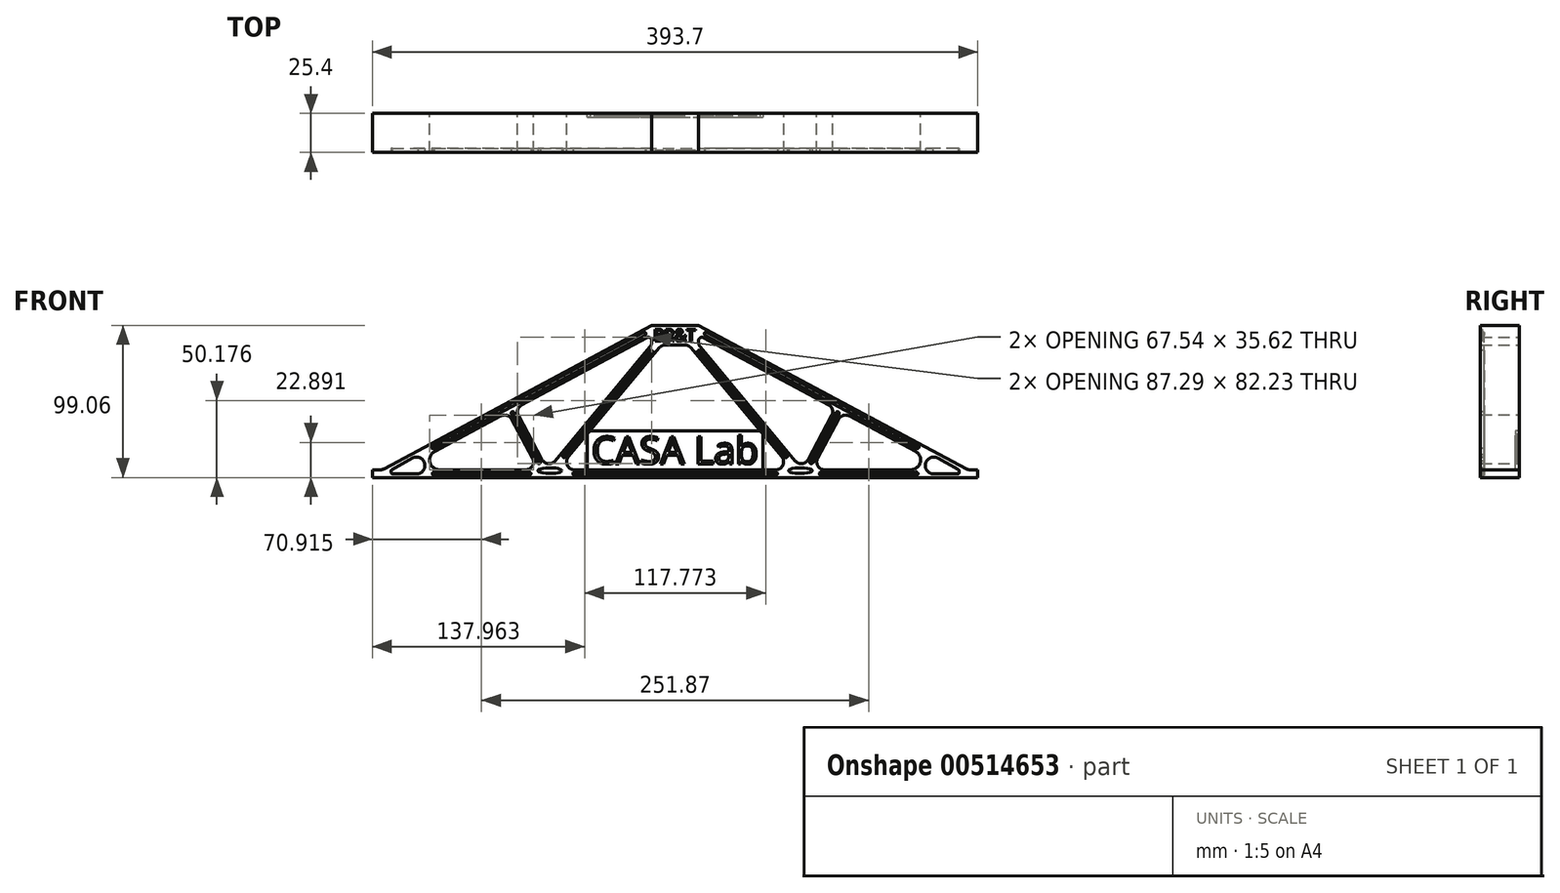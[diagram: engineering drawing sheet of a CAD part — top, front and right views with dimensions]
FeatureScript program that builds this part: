
annotation { "Feature Type Name" : "Feature", "Feature Type Description" : "" }
export const myFeature = defineFeature(function(context is Context, id is Id, definition is map)
    precondition{}
    {
        {
            var Q0;
            Q0=qCreatedBy(makeId("Front.planeOp"),FACE);
            var sketch = newSketch(context, id + "F0", { "sketchPlane" : qUnion([Q0])});
            skLineSegment(sketch, "E0", {"start": v(-15.24, 99.06) * mm, "end": v(0, 99.06) * mm});
            skLineSegment(sketch, "E1.top", {"start": v(-6.25, 86.36) * mm, "end": v(0, 86.36) * mm});
            skLineSegment(sketch, "E1.left", {"start": v(-15.24, 89.18) * mm, "end": v(-15.24, 88.2) * mm});
            skLineSegment(sketch, "E1.right", {"start": v(0, 99.06) * mm, "end": v(0, 86.36) * mm});
            skLineSegment(sketch, "E2.bottom", {"start": v(0, 0) * mm, "end": v(-196.85, 0) * mm});
            skLineSegment(sketch, "E2.top", {"start": v(-97.24, 5.08) * mm, "end": v(-153.38, 5.08) * mm});
            skLineSegment(sketch, "E2.left", {"start": v(0, 0) * mm, "end": v(0, 5.08) * mm});
            skLineSegment(sketch, "E2.right", {"start": v(-196.85, 0) * mm, "end": v(-196.85, 5.08) * mm});
            skLineSegment(sketch, "E3", {"start": v(-15.24, 99.06) * mm, "end": v(-189.38, 5.68) * mm});
            skLineSegment(sketch, "E4", {"start": v(-99.88, 47.32) * mm, "end": v(-18.35, 91.04) * mm});
            skLineSegment(sketch, "E5", {"start": v(-10.15, 84.53) * mm, "end": v(-69.43, 13.41) * mm});
            skLineSegment(sketch, "E6", {"start": v(-76.38, 5.08) * mm, "end": v(-82.99, 5.08) * mm});
            skLineSegment(sketch, "E7", {"start": v(-78.17, 10.86) * mm, "end": v(-16.42, 84.95) * mm});
            skLineSegment(sketch, "E8", {"start": v(-86.55, 11.72) * mm, "end": v(-101.95, 40.45) * mm});
            skLineSegment(sketch, "E9", {"start": v(-106.43, 38.05) * mm, "end": v(-92.77, 12.56) * mm});
            skLineSegment(sketch, "E10", {"start": v(-88.75, 5.08) * mm, "end": v(-82.99, 5.08) * mm});
            skArc(sketch, "E11.filletArc", {"start": v(-156.38, 17.03) * mm, "mid": v(-159.54, 9.88) * mm, "end": v(-153.38, 5.08) * mm});
            skLineSegment(sketch, "E12", {"start": v(-196.85, 5.08) * mm, "end": v(-191.78, 5.08) * mm});
            skPoint(sketch, "E13.newPointA", {"position": v(-15.24, 92.71) * mm});
            skPoint(sketch, "E13.newPointB", {"position": v(-15.24, 99.06) * mm});
            skArc(sketch, "E13.filletArc", {"start": v(-15.24, 89.18) * mm, "mid": v(-16.27, 91) * mm, "end": v(-18.35, 91.04) * mm});
            skPoint(sketch, "E14.visualSharp", {"position": v(-82.99, 5.08) * mm});
            skArc(sketch, "E14.filletArc", {"start": v(-86.55, 11.72) * mm, "mid": v(-82.58, 9.06) * mm, "end": v(-78.17, 10.86) * mm});
            skArc(sketch, "E15.filletArc", {"start": v(-99.88, 47.32) * mm, "mid": v(-102.34, 44.32) * mm, "end": v(-101.95, 40.45) * mm});
            skLineSegment(sketch, "E16", {"start": v(-113.3, 40.12) * mm, "end": v(-156.38, 17.03) * mm});
            skPoint(sketch, "E17.visualSharp", {"position": v(-108.83, 42.52) * mm});
            skArc(sketch, "E17.filletArc", {"start": v(-106.43, 38.05) * mm, "mid": v(-109.44, 40.5) * mm, "end": v(-113.3, 40.12) * mm});
            skPoint(sketch, "E18.newPointA", {"position": v(-88.75, 5.08) * mm});
            skArc(sketch, "E18.filletArc", {"start": v(-97.24, 5.08) * mm, "mid": v(-92.88, 7.55) * mm, "end": v(-92.77, 12.56) * mm});
            skLineSegment(sketch, "E19", {"start": v(-65.53, 5.08) * mm, "end": v(0, 5.08) * mm});
            skPoint(sketch, "E20.visualSharp", {"position": v(-76.38, 5.08) * mm});
            skArc(sketch, "E20.filletArc", {"start": v(-69.43, 13.41) * mm, "mid": v(-70.13, 8) * mm, "end": v(-65.53, 5.08) * mm});
            skArc(sketch, "E21.filletArc", {"start": v(-6.25, 86.36) * mm, "mid": v(-8.4, 85.88) * mm, "end": v(-10.15, 84.53) * mm});
            skLineSegment(sketch, "E22.MirrorCS", {"start": v(15.24, 89.18) * mm, "end": v(15.24, 88.2) * mm});
            skArc(sketch, "E23.MirrorCS", {"start": v(15.24, 89.18) * mm, "mid": v(16.27, 91) * mm, "end": v(18.35, 91.04) * mm});
            skArc(sketch, "E24.MirrorCS", {"start": v(86.55, 11.72) * mm, "mid": v(82.58, 9.06) * mm, "end": v(78.17, 10.86) * mm});
            skLineSegment(sketch, "E25.MirrorCS", {"start": v(196.85, 5.08) * mm, "end": v(191.78, 5.08) * mm});
            skLineSegment(sketch, "E26.MirrorCS", {"start": v(76.38, 5.08) * mm, "end": v(82.99, 5.08) * mm});
            skArc(sketch, "E27.MirrorCS", {"start": v(6.25, 86.36) * mm, "mid": v(8.4, 85.88) * mm, "end": v(10.15, 84.53) * mm});
            skLineSegment(sketch, "E28.MirrorCS", {"start": v(196.85, 0) * mm, "end": v(196.85, 5.08) * mm});
            skArc(sketch, "E29.MirrorCS", {"start": v(106.43, 38.05) * mm, "mid": v(109.44, 40.5) * mm, "end": v(113.3, 40.12) * mm});
            skLineSegment(sketch, "E30.MirrorCS", {"start": v(6.25, 86.36) * mm, "end": v(0, 86.36) * mm});
            skLineSegment(sketch, "E31.MirrorCS", {"start": v(88.75, 5.08) * mm, "end": v(82.99, 5.08) * mm});
            skArc(sketch, "E32.MirrorCS", {"start": v(97.24, 5.08) * mm, "mid": v(92.88, 7.55) * mm, "end": v(92.77, 12.56) * mm});
            skArc(sketch, "E33.MirrorCS", {"start": v(99.88, 47.32) * mm, "mid": v(102.34, 44.32) * mm, "end": v(101.95, 40.45) * mm});
            skArc(sketch, "E34.MirrorCS", {"start": v(69.43, 13.41) * mm, "mid": v(70.13, 8) * mm, "end": v(65.53, 5.08) * mm});
            skLineSegment(sketch, "E35.MirrorCS", {"start": v(15.24, 99.06) * mm, "end": v(0, 99.06) * mm});
            skPoint(sketch, "E36.MirrorP", {"position": v(15.24, 92.71) * mm});
            skLineSegment(sketch, "E37.MirrorCS", {"start": v(97.24, 5.08) * mm, "end": v(153.38, 5.08) * mm});
            skPoint(sketch, "E38.MirrorP", {"position": v(76.38, 5.08) * mm});
            skLineSegment(sketch, "E39.MirrorCS", {"start": v(0, 0) * mm, "end": v(196.85, 0) * mm});
            skLineSegment(sketch, "E40.MirrorCS", {"start": v(65.53, 5.08) * mm, "end": v(0, 5.08) * mm});
            skLineSegment(sketch, "E41.MirrorCS", {"start": v(113.3, 40.12) * mm, "end": v(156.38, 17.03) * mm});
            skLineSegment(sketch, "E42.MirrorCS", {"start": v(99.88, 47.32) * mm, "end": v(18.35, 91.04) * mm});
            skLineSegment(sketch, "E43.MirrorCS", {"start": v(10.15, 84.53) * mm, "end": v(69.43, 13.41) * mm});
            skLineSegment(sketch, "E44.MirrorCS", {"start": v(15.24, 99.06) * mm, "end": v(189.38, 5.68) * mm});
            skPoint(sketch, "E45.MirrorP", {"position": v(108.83, 42.52) * mm});
            skLineSegment(sketch, "E46.MirrorCS", {"start": v(106.43, 38.05) * mm, "end": v(92.77, 12.56) * mm});
            skLineSegment(sketch, "E47.MirrorCS", {"start": v(86.55, 11.72) * mm, "end": v(101.95, 40.45) * mm});
            skPoint(sketch, "E48.MirrorP", {"position": v(88.75, 5.08) * mm});
            skArc(sketch, "E49.MirrorCS", {"start": v(156.38, 17.03) * mm, "mid": v(159.54, 9.88) * mm, "end": v(153.38, 5.08) * mm});
            skPoint(sketch, "E50.MirrorP", {"position": v(82.99, 5.08) * mm});
            skPoint(sketch, "E51.MirrorP", {"position": v(15.24, 99.06) * mm});
            skLineSegment(sketch, "E52.MirrorCS", {"start": v(78.17, 10.86) * mm, "end": v(16.42, 84.95) * mm});
            skPoint(sketch, "E53.visualSharp", {"position": v(-15.24, 86.36) * mm});
            skArc(sketch, "E53.filletArc", {"start": v(-16.42, 84.95) * mm, "mid": v(-15.54, 86.47) * mm, "end": v(-15.24, 88.2) * mm});
            skPoint(sketch, "E54.visualSharp", {"position": v(15.24, 86.36) * mm});
            skArc(sketch, "E54.filletArc", {"start": v(15.24, 88.2) * mm, "mid": v(15.54, 86.47) * mm, "end": v(16.42, 84.95) * mm});
            skPoint(sketch, "E55.visualSharp", {"position": v(-190.5, 5.08) * mm});
            skArc(sketch, "E55.filletArc", {"start": v(-191.78, 5.08) * mm, "mid": v(-190.54, 5.23) * mm, "end": v(-189.38, 5.68) * mm});
            skPoint(sketch, "E56.visualSharp", {"position": v(190.5, 5.08) * mm});
            skArc(sketch, "E56.filletArc", {"start": v(189.38, 5.68) * mm, "mid": v(190.54, 5.23) * mm, "end": v(191.78, 5.08) * mm});
            skSolve(sketch);
        }
        {
            var Q0;
            Q0=makeQuery(id+"F0.imprint","IMPRINT",FACE,{"disambiguationData":[TD([[makeQuery(id+"F0.imprint","IMPRINT",EDGE,{"derivedFrom":sQuery(id+"F0.wireOp",EDGE,"E0")}),-1.0]])]});
            var Q1;
            Q1=makeQuery(id+"F0.imprint","IMPRINT",FACE,{"disambiguationData":[TD([[makeQuery(id+"F0.imprint","IMPRINT",EDGE,{"derivedFrom":sQuery(id+"F0.wireOp",EDGE,"E22.MirrorCS")}),-1.0]])]});
            extrude(context, id + "F1", {"entities" : qUnion([Q0, Q1]), "depth" : 25.4 * mm, "offsetDistance" : 25.4 * mm});
        }
        {
            var Q0;
            Q0=makeQuery(id+"F1.opExtrude","CAP_FACE",FACE,{"disambiguationData":[OSD([sQuery(id+"F0.wireOp",EDGE,"E0"),sQuery(id+"F0.wireOp",EDGE,"E1.top"),sQuery(id+"F0.wireOp",EDGE,"E1.left"),sQuery(id+"F0.wireOp",EDGE,"E2.bottom"),sQuery(id+"F0.wireOp",EDGE,"E2.top"),sQuery(id+"F0.wireOp",EDGE,"E2.right"),sQuery(id+"F0.wireOp",EDGE,"E3"),sQuery(id+"F0.wireOp",EDGE,"E4"),sQuery(id+"F0.wireOp",EDGE,"E5"),sQuery(id+"F0.wireOp",EDGE,"E7"),sQuery(id+"F0.wireOp",EDGE,"E8"),sQuery(id+"F0.wireOp",EDGE,"E9"),sQuery(id+"F0.wireOp",EDGE,"E11.filletArc"),sQuery(id+"F0.wireOp",EDGE,"E12"),sQuery(id+"F0.wireOp",EDGE,"E13.filletArc"),sQuery(id+"F0.wireOp",EDGE,"E14.filletArc"),sQuery(id+"F0.wireOp",EDGE,"E15.filletArc"),sQuery(id+"F0.wireOp",EDGE,"E16"),sQuery(id+"F0.wireOp",EDGE,"E17.filletArc"),sQuery(id+"F0.wireOp",EDGE,"E18.filletArc"),sQuery(id+"F0.wireOp",EDGE,"E19"),sQuery(id+"F0.wireOp",EDGE,"E20.filletArc"),sQuery(id+"F0.wireOp",EDGE,"E21.filletArc"),sQuery(id+"F0.wireOp",EDGE,"E22.MirrorCS"),sQuery(id+"F0.wireOp",EDGE,"E23.MirrorCS"),sQuery(id+"F0.wireOp",EDGE,"E24.MirrorCS"),sQuery(id+"F0.wireOp",EDGE,"E25.MirrorCS"),sQuery(id+"F0.wireOp",EDGE,"E27.MirrorCS"),sQuery(id+"F0.wireOp",EDGE,"E28.MirrorCS"),sQuery(id+"F0.wireOp",EDGE,"E29.MirrorCS"),sQuery(id+"F0.wireOp",EDGE,"E30.MirrorCS"),sQuery(id+"F0.wireOp",EDGE,"E32.MirrorCS"),sQuery(id+"F0.wireOp",EDGE,"E33.MirrorCS"),sQuery(id+"F0.wireOp",EDGE,"E34.MirrorCS"),sQuery(id+"F0.wireOp",EDGE,"E37.MirrorCS"),sQuery(id+"F0.wireOp",EDGE,"E39.MirrorCS"),sQuery(id+"F0.wireOp",EDGE,"E40.MirrorCS"),sQuery(id+"F0.wireOp",EDGE,"E41.MirrorCS"),sQuery(id+"F0.wireOp",EDGE,"E42.MirrorCS"),sQuery(id+"F0.wireOp",EDGE,"E43.MirrorCS"),sQuery(id+"F0.wireOp",EDGE,"E44.MirrorCS"),sQuery(id+"F0.wireOp",EDGE,"E46.MirrorCS"),sQuery(id+"F0.wireOp",EDGE,"E47.MirrorCS"),sQuery(id+"F0.wireOp",EDGE,"E35.MirrorCS"),sQuery(id+"F0.wireOp",EDGE,"E49.MirrorCS"),sQuery(id+"F0.wireOp",EDGE,"E52.MirrorCS")])],"isStart":false});
            var sketch = newSketch(context, id + "F2", { "sketchPlane" : qUnion([Q0])});
            skText(sketch, "E57", { "text": "BR&T", "fontName": "OpenSans-Regular.ttf"});
            const initialGuessF2  = {"E57": [-0.01397, 0.0888, 1, 0, 0.00772]};
            skSetInitialGuess(sketch, initialGuessF2);
            skSolve(sketch);
        }
        {
            var Q0;
            Q0 = qSketchRegion(id + "F2", true);
            extrude(context, id + "F3", {"entities" : qUnion([Q0]), "operationType" : NewBodyOperationType.REMOVE, "oppositeDirection" : true, "depth" : 1.27 * mm, "offsetDistance" : 25.4 * mm});
        }
        {
            var Q0;
            Q0=qCreatedBy(makeId("Front.planeOp"),FACE);
            var sketch = newSketch(context, id + "F4", { "sketchPlane" : qUnion([Q0])});
            skLineSegment(sketch, "E58.bottom", {"start": v(-57.15, 5.08) * mm, "end": v(0, 5.08) * mm});
            skLineSegment(sketch, "E58.top", {"start": v(-57.15, 30.48) * mm, "end": v(0, 30.48) * mm});
            skLineSegment(sketch, "E58.left", {"start": v(-57.15, 5.08) * mm, "end": v(-57.15, 30.48) * mm});
            skLineSegment(sketch, "E58.right", {"start": v(0, 5.08) * mm, "end": v(0, 30.48) * mm});
            skLineSegment(sketch, "E59.MirrorCS", {"start": v(57.15, 5.08) * mm, "end": v(57.15, 30.48) * mm});
            skLineSegment(sketch, "E60.MirrorCS", {"start": v(57.15, 30.48) * mm, "end": v(0, 30.48) * mm});
            skLineSegment(sketch, "E61.MirrorCS", {"start": v(57.15, 5.08) * mm, "end": v(0, 5.08) * mm});
            skSolve(sketch);
        }
        {
            var Q0;
            Q0 = qSketchRegion(id + "F4", true);
            extrude(context, id + "F5", {"entities" : qUnion([Q0]), "operationType" : NewBodyOperationType.ADD, "depth" : 2.54 * mm, "offsetDistance" : 25.4 * mm});
        }
        {
            var Q0;
            Q0=makeQuery(id+"F5.opExtrude","CAP_FACE",FACE,{"disambiguationData":[OSD([sQuery(id+"F4.wireOp",EDGE,"E58.bottom"),sQuery(id+"F4.wireOp",EDGE,"E58.top"),sQuery(id+"F4.wireOp",EDGE,"E58.left"),sQuery(id+"F4.wireOp",EDGE,"E59.MirrorCS"),sQuery(id+"F4.wireOp",EDGE,"E60.MirrorCS"),sQuery(id+"F4.wireOp",EDGE,"E61.MirrorCS")])],"isStart":false});
            var sketch = newSketch(context, id + "F6", { "sketchPlane" : qUnion([Q0])});
            skText(sketch, "E62", { "text": "CASA Lab", "fontName": "OpenSans-Regular.ttf"});
            const initialGuessF6  = {"E62": [-0.05436, 0.0089, 1, 0, 0.01778]};
            skSetInitialGuess(sketch, initialGuessF6);
            skSolve(sketch);
        }
        {
            var Q0;
            Q0 = qSketchRegion(id + "F6", true);
            extrude(context, id + "F7", {"entities" : qUnion([Q0]), "operationType" : NewBodyOperationType.REMOVE, "oppositeDirection" : true, "depth" : 1.27 * mm, "offsetDistance" : 25.4 * mm});
        }
        {
            var Q0;
            {var subQ0=sQuery(id+"F0.wireOp",EDGE,"E32.MirrorCS");var subQ1=sQuery(id+"F0.wireOp",EDGE,"E20.filletArc");var subQ2=sQuery(id+"F0.wireOp",EDGE,"E29.MirrorCS");var subQ3=sQuery(id+"F0.wireOp",EDGE,"E40.MirrorCS");var subQ4=sQuery(id+"F0.wireOp",EDGE,"E19");var subQ5=sQuery(id+"F0.wireOp",EDGE,"E28.MirrorCS");var subQ6=sQuery(id+"F0.wireOp",EDGE,"E18.filletArc");var subQ7=sQuery(id+"F0.wireOp",EDGE,"E17.filletArc");var subQ8=sQuery(id+"F0.wireOp",EDGE,"E16");var subQ9=sQuery(id+"F0.wireOp",EDGE,"E24.MirrorCS");var subQ10=sQuery(id+"F0.wireOp",EDGE,"E15.filletArc");var subQ11=sQuery(id+"F0.wireOp",EDGE,"E14.filletArc");var subQ12=sQuery(id+"F0.wireOp",EDGE,"E13.filletArc");var subQ13=sQuery(id+"F0.wireOp",EDGE,"E12");var subQ14=sQuery(id+"F0.wireOp",EDGE,"E11.filletArc");var subQ15=sQuery(id+"F0.wireOp",EDGE,"E9");var subQ16=sQuery(id+"F0.wireOp",EDGE,"E8");var subQ17=sQuery(id+"F0.wireOp",EDGE,"E39.MirrorCS");var subQ18=sQuery(id+"F0.wireOp",EDGE,"E2.bottom");var subQ19=sQuery(id+"F0.wireOp",EDGE,"E1.left");var subQ20=sQuery(id+"F0.wireOp",EDGE,"E30.MirrorCS");var subQ21=sQuery(id+"F0.wireOp",EDGE,"E1.top");var subQ22=sQuery(id+"F0.wireOp",EDGE,"E35.MirrorCS");var subQ23=sQuery(id+"F0.wireOp",EDGE,"E0");var subQ24=sQuery(id+"F0.wireOp",EDGE,"E2.top");var subQ25=sQuery(id+"F0.wireOp",EDGE,"E2.right");var subQ26=sQuery(id+"F0.wireOp",EDGE,"E3");var subQ27=sQuery(id+"F0.wireOp",EDGE,"E4");var subQ28=sQuery(id+"F0.wireOp",EDGE,"E5");var subQ29=sQuery(id+"F0.wireOp",EDGE,"E7");var subQ30=sQuery(id+"F0.wireOp",EDGE,"E33.MirrorCS");var subQ31=sQuery(id+"F0.wireOp",EDGE,"E21.filletArc");var subQ32=sQuery(id+"F0.wireOp",EDGE,"E34.MirrorCS");var subQ33=sQuery(id+"F0.wireOp",EDGE,"E22.MirrorCS");var subQ34=sQuery(id+"F0.wireOp",EDGE,"E37.MirrorCS");var subQ35=sQuery(id+"F0.wireOp",EDGE,"E23.MirrorCS");var subQ36=sQuery(id+"F0.wireOp",EDGE,"E41.MirrorCS");var subQ37=sQuery(id+"F0.wireOp",EDGE,"E42.MirrorCS");var subQ38=sQuery(id+"F0.wireOp",EDGE,"E25.MirrorCS");var subQ39=sQuery(id+"F0.wireOp",EDGE,"E43.MirrorCS");var subQ40=sQuery(id+"F0.wireOp",EDGE,"E27.MirrorCS");var subQ41=sQuery(id+"F0.wireOp",EDGE,"E44.MirrorCS");var subQ42=sQuery(id+"F0.wireOp",EDGE,"E46.MirrorCS");var subQ43=sQuery(id+"F0.wireOp",EDGE,"E47.MirrorCS");var subQ44=sQuery(id+"F0.wireOp",EDGE,"E49.MirrorCS");var subQ45=sQuery(id+"F0.wireOp",EDGE,"E52.MirrorCS");var subQ46=sQuery(id+"F0.wireOp",EDGE,"E53.filletArc");var subQ47=sQuery(id+"F0.wireOp",EDGE,"E54.filletArc");var subQ48=sQuery(id+"F0.wireOp",EDGE,"E55.filletArc");var subQ49=sQuery(id+"F0.wireOp",EDGE,"E56.filletArc");Q0=makeQuery(id+"F3.boolean.opBoolean","SPLIT",FACE,{"disambiguationData":[TD([makeQuery(id+"F1.opExtrude","SWEPT_FACE",FACE,{"disambiguationData":[OSD([subQ19])]})])],"derivedFrom":makeQuery(id+"F1.opExtrude","CAP_FACE",FACE,{"disambiguationData":[OSD([subQ23,subQ21,subQ19,subQ18,subQ24,subQ25,subQ26,subQ27,subQ28,subQ29,subQ16,subQ15,subQ14,subQ13,subQ12,subQ11,subQ10,subQ8,subQ7,subQ6,subQ4,subQ1,subQ31,subQ33,subQ35,subQ9,subQ38,subQ40,subQ5,subQ2,subQ20,subQ0,subQ30,subQ32,subQ34,subQ17,subQ3,subQ36,subQ37,subQ39,subQ41,subQ42,subQ43,subQ22,subQ44,subQ45,subQ46,subQ47,subQ48,subQ49])],"isStart":false})});}
            var sketch = newSketch(context, id + "F8", { "sketchPlane" : qUnion([Q0])});
            skEllipse(sketch, "E63", {"center": v(-81.48, 4.48) * mm, "majorRadius": 7.68 * mm, "minorRadius": 1.86 * mm, "majorAxis": v(1, 0)});
            skLineSegment(sketch, "E64", {"start": v(-157.1, 18.96) * mm, "end": v(-19.46, 92.76) * mm});
            skLineSegment(sketch, "E65", {"start": v(-157.1, 18.96) * mm, "end": v(-158.06, 20.75) * mm});
            skLineSegment(sketch, "E66", {"start": v(-158.06, 20.75) * mm, "end": v(-20.56, 94.48) * mm});
            skLineSegment(sketch, "E67", {"start": v(-20.56, 94.48) * mm, "end": v(-19.46, 92.76) * mm});
            skArc(sketch, "E68", {"start": v(-158.06, 20.75) * mm, "mid": v(-158.48, 19.37) * mm, "end": v(-157.1, 18.96) * mm});
            skArc(sketch, "E69", {"start": v(-19.46, 92.76) * mm, "mid": v(-19.21, 94.13) * mm, "end": v(-20.56, 94.48) * mm});
            skLineSegment(sketch, "E70", {"start": v(-104.72, 42.37) * mm, "end": v(-87.68, 10.6) * mm});
            skLineSegment(sketch, "E71", {"start": v(-104.72, 42.37) * mm, "end": v(-106.5, 41.41) * mm});
            skLineSegment(sketch, "E72", {"start": v(-106.5, 41.41) * mm, "end": v(-89.44, 9.58) * mm});
            skLineSegment(sketch, "E73", {"start": v(-89.44, 9.58) * mm, "end": v(-87.68, 10.6) * mm});
            skArc(sketch, "E74", {"start": v(-104.72, 42.37) * mm, "mid": v(-106.1, 42.79) * mm, "end": v(-106.5, 41.41) * mm});
            skArc(sketch, "E75", {"start": v(-89.44, 9.58) * mm, "mid": v(-88.03, 9.18) * mm, "end": v(-87.68, 10.6) * mm});
            skLineSegment(sketch, "E76", {"start": v(-72.98, 14.7) * mm, "end": v(-16.42, 82.57) * mm});
            skLineSegment(sketch, "E77", {"start": v(-16.42, 82.57) * mm, "end": v(-14.86, 81.27) * mm});
            skLineSegment(sketch, "E78", {"start": v(-14.86, 81.27) * mm, "end": v(-71.41, 13.41) * mm});
            skLineSegment(sketch, "E79", {"start": v(-71.41, 13.41) * mm, "end": v(-72.98, 14.7) * mm});
            skArc(sketch, "E80", {"start": v(-14.86, 81.27) * mm, "mid": v(-14.99, 82.7) * mm, "end": v(-16.42, 82.57) * mm});
            skArc(sketch, "E81", {"start": v(-72.98, 14.7) * mm, "mid": v(-72.84, 13.28) * mm, "end": v(-71.41, 13.41) * mm});
            skLineSegment(sketch, "E82", {"start": v(-156.81, 3.56) * mm, "end": v(-94.84, 3.56) * mm});
            skLineSegment(sketch, "E83", {"start": v(-94.84, 3.56) * mm, "end": v(-94.84, 1.52) * mm});
            skLineSegment(sketch, "E84", {"start": v(-94.84, 1.52) * mm, "end": v(-156.94, 1.52) * mm});
            skLineSegment(sketch, "E85", {"start": v(-156.94, 1.52) * mm, "end": v(-156.81, 3.56) * mm});
            skArc(sketch, "E86", {"start": v(-156.81, 3.56) * mm, "mid": v(-157.96, 2.6) * mm, "end": v(-156.94, 1.52) * mm});
            skArc(sketch, "E87", {"start": v(-94.84, 1.52) * mm, "mid": v(-93.83, 2.54) * mm, "end": v(-94.84, 3.56) * mm});
            skLineSegment(sketch, "E88", {"start": v(-183.96, 5.45) * mm, "end": v(-171, 12.66) * mm});
            skLineSegment(sketch, "E89", {"start": v(-184.04, 2.35) * mm, "end": v(-167.52, 2.35) * mm});
            skArc(sketch, "E90", {"start": v(-183.96, 5.45) * mm, "mid": v(-184.89, 3.92) * mm, "end": v(-184.04, 2.35) * mm});
            skArc(sketch, "E91", {"start": v(-167.52, 2.35) * mm, "mid": v(-163.07, 9.6) * mm, "end": v(-171, 12.66) * mm});
            skLineSegment(sketch, "E92", {"start": v(0, 3.56) * mm, "end": v(-65.53, 3.56) * mm});
            skLineSegment(sketch, "E93", {"start": v(-65.53, 3.56) * mm, "end": v(-65.53, 1.52) * mm});
            skLineSegment(sketch, "E94", {"start": v(-65.53, 1.52) * mm, "end": v(0, 1.52) * mm});
            skArc(sketch, "E95", {"start": v(-65.53, 3.56) * mm, "mid": v(-66.54, 2.54) * mm, "end": v(-65.53, 1.52) * mm});
            skArc(sketch, "E96.MirrorCS", {"start": v(72.98, 14.7) * mm, "mid": v(72.84, 13.28) * mm, "end": v(71.41, 13.41) * mm});
            skLineSegment(sketch, "E97.MirrorCS", {"start": v(16.42, 82.57) * mm, "end": v(14.86, 81.27) * mm});
            skArc(sketch, "E98.MirrorCS", {"start": v(14.86, 81.27) * mm, "mid": v(14.99, 82.7) * mm, "end": v(16.42, 82.57) * mm});
            skLineSegment(sketch, "E99.MirrorCS", {"start": v(157.1, 18.96) * mm, "end": v(158.06, 20.75) * mm});
            skLineSegment(sketch, "E100.MirrorCS", {"start": v(71.41, 13.41) * mm, "end": v(72.98, 14.7) * mm});
            skLineSegment(sketch, "E101.MirrorCS", {"start": v(156.94, 1.52) * mm, "end": v(156.81, 3.56) * mm});
            skArc(sketch, "E102.MirrorCS", {"start": v(158.06, 20.75) * mm, "mid": v(158.48, 19.37) * mm, "end": v(157.1, 18.96) * mm});
            skLineSegment(sketch, "E103.MirrorCS", {"start": v(94.84, 3.56) * mm, "end": v(94.84, 1.52) * mm});
            skLineSegment(sketch, "E104.MirrorCS", {"start": v(104.72, 42.37) * mm, "end": v(106.5, 41.41) * mm});
            skArc(sketch, "E105.MirrorCS", {"start": v(94.84, 1.52) * mm, "mid": v(93.83, 2.54) * mm, "end": v(94.84, 3.56) * mm});
            skArc(sketch, "E106.MirrorCS", {"start": v(156.81, 3.56) * mm, "mid": v(157.96, 2.6) * mm, "end": v(156.94, 1.52) * mm});
            skLineSegment(sketch, "E107.MirrorCS", {"start": v(89.44, 9.58) * mm, "end": v(87.68, 10.6) * mm});
            skArc(sketch, "E108.MirrorCS", {"start": v(104.72, 42.37) * mm, "mid": v(106.1, 42.79) * mm, "end": v(106.5, 41.41) * mm});
            skArc(sketch, "E109.MirrorCS", {"start": v(65.53, 3.56) * mm, "mid": v(66.54, 2.54) * mm, "end": v(65.53, 1.52) * mm});
            skLineSegment(sketch, "E110.MirrorCS", {"start": v(20.56, 94.48) * mm, "end": v(19.46, 92.76) * mm});
            skLineSegment(sketch, "E111.MirrorCS", {"start": v(65.53, 3.56) * mm, "end": v(65.53, 1.52) * mm});
            skArc(sketch, "E112.MirrorCS", {"start": v(19.46, 92.76) * mm, "mid": v(19.21, 94.13) * mm, "end": v(20.56, 94.48) * mm});
            skArc(sketch, "E113.MirrorCS", {"start": v(89.44, 9.58) * mm, "mid": v(88.03, 9.18) * mm, "end": v(87.68, 10.6) * mm});
            skArc(sketch, "E114.MirrorCS", {"start": v(183.96, 5.45) * mm, "mid": v(184.89, 3.92) * mm, "end": v(184.04, 2.35) * mm});
            skLineSegment(sketch, "E115.MirrorCS", {"start": v(72.98, 14.7) * mm, "end": v(16.42, 82.57) * mm});
            skLineSegment(sketch, "E116.MirrorCS", {"start": v(14.86, 81.27) * mm, "end": v(71.41, 13.41) * mm});
            skEllipse(sketch, "E117.MirrorC", {"center": v(81.48, 4.48) * mm, "majorRadius": 7.68 * mm, "minorRadius": 1.86 * mm, "majorAxis": v(-1, 0)});
            skLineSegment(sketch, "E118.MirrorCS", {"start": v(157.1, 18.96) * mm, "end": v(19.46, 92.76) * mm});
            skLineSegment(sketch, "E119.MirrorCS", {"start": v(106.5, 41.41) * mm, "end": v(89.44, 9.58) * mm});
            skLineSegment(sketch, "E120.MirrorCS", {"start": v(158.06, 20.75) * mm, "end": v(20.56, 94.48) * mm});
            skLineSegment(sketch, "E121.MirrorCS", {"start": v(183.96, 5.45) * mm, "end": v(171, 12.66) * mm});
            skLineSegment(sketch, "E122.MirrorCS", {"start": v(65.53, 1.52) * mm, "end": v(0, 1.52) * mm});
            skArc(sketch, "E123.MirrorCS", {"start": v(167.52, 2.35) * mm, "mid": v(163.07, 9.6) * mm, "end": v(171, 12.66) * mm});
            skLineSegment(sketch, "E124.MirrorCS", {"start": v(0, 3.56) * mm, "end": v(65.53, 3.56) * mm});
            skLineSegment(sketch, "E125.MirrorCS", {"start": v(104.72, 42.37) * mm, "end": v(87.68, 10.6) * mm});
            skLineSegment(sketch, "E126.MirrorCS", {"start": v(94.84, 1.52) * mm, "end": v(156.94, 1.52) * mm});
            skLineSegment(sketch, "E127.MirrorCS", {"start": v(156.81, 3.56) * mm, "end": v(94.84, 3.56) * mm});
            skLineSegment(sketch, "E128.MirrorCS", {"start": v(184.04, 2.35) * mm, "end": v(167.52, 2.35) * mm});
            skSolve(sketch);
        }
        {
            var Q0;
            Q0 = qSketchRegion(id + "F8", true);
            extrude(context, id + "F9", {"entities" : qUnion([Q0]), "operationType" : NewBodyOperationType.REMOVE, "oppositeDirection" : true, "depth" : 2.54 * mm, "offsetDistance" : 25.4 * mm});
        }
    });
